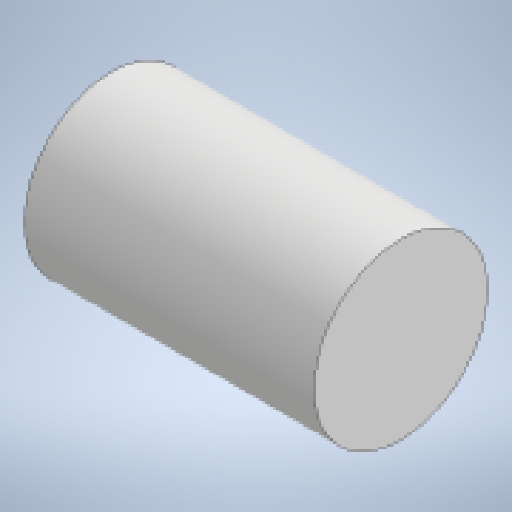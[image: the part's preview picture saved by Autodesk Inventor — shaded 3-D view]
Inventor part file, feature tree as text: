
AUTODESK INVENTOR PART (.ipt)
format: ipt  version: 2025 (Build 290162010, 162A)  size: 126,976 bytes
history: native  units: mm
features: extrude x1, sketch x1
ambient origin geometry x8: Origin, YZ Plane, XZ Plane, XY Plane, X Axis, Y Axis, Z Axis, Center Point
bodies: Volumenkörper1 (feature_tree)
feature tree (2):
  extrude  "Extrusion1"  Depth=0.2mm
  sketch  "Skizze1"  dims[d1=0.5mm d2=0.0mm d3=0.2mm d4=0.2mm]
